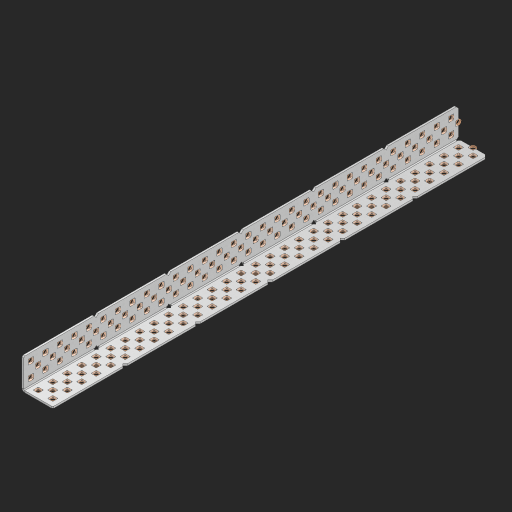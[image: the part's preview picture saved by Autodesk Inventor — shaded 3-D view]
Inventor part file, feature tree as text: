
AUTODESK INVENTOR PART (.ipt)
format: ipt  version: 2023 (Build 270158000, 158)  size: 1,938,432 bytes
history: native  units: in
note: dims shown in document units (in); Inventor stores cm internally (conversion verified against a paired STEP export)
features: other x186, extrude x178, sheet_metal_op x8, sketch x7, pattern_linear x2, mirror x1, chamfer x1
ambient origin geometry x8: Origin, YZ Plane, XZ Plane, XY Plane, X Axis, Y Axis, Z Axis, Center Point
bodies: Solid1 (feature_tree), Body (feature_tree)
feature tree (383):
  sheet_metal_op  "Flanges"
  sheet_metal_op  "Body Pattern"
  pattern_linear  "Center Pattern"  Spacing1=1.0in  [1 undecoded]
  other  "Arc Length"
  pattern_linear  "Notch Pattern"  Spacing1=0.25in  [1 undecoded]
  other  "Diagonal Plane"
  mirror  "Everything Mirrored"
  chamfer  "End Chamfer"
  sketch  "Sketch1"  dims[d0=1.0in]
  other  "Plate1"
  sketch  "Sketch2"  dims[d1=15.0in]
  other  "Plate2"
  sheet_metal_op  "Bend1"
  sheet_metal_op  "Corner1"
  sketch  "Sketch8"  dims[d2=0.0625in]
  sketch  "Sketch9"  dims[d3=0.0625in]
  other  "Srf91"
  sheet_metal_op  "Body Pattern Sketch"
  other  "Srf92"
  sketch  "Sketch13"  dims[d4=0.0312in]
  sketch  "Sketch15"  dims[d5=0.125in]
  sketch  "Sketch16"  dims[d6=0.0625in d7=1.0in d8=90.0deg d9=0.0312in d10=0.25in d11=0.0625in d12=0.0625in d49=0.182in d50=0.02in d52=0.25in d53=0.0625in d54=0.0in d55=0.172in d56=1.0in d57=0.0in d60=11.811in d62=0.5in d63=0.7874in d65=0.5in d85=0.1473in d86=0.1782in d89=0.0625in d90=0.0in d91=0.04in d92=0.0491in d95=2.5in d96=0.04in d97=0.25in d98=45.0deg d99=0.25in d106=0.182in d107=0.02in d108=0.5in d110=0.0625in d111=0.0in d112=0.172in d113=0.5in d114=0.0in d117=0.5in d123=0.25in d125=0.25in d126=0.0491in d127=0.1473in d128=0.08in d129=0.04in d130=2.5in]
  other  "Srf786"
  other  "Srf856"
  other  "Srf857"
  other  "Srf858"
  other  "Srf859"
  other  "Srf860"
  other  "Srf861"
  other  "Srf889"
  other  "Srf890"
  other  "Srf891"
  other  "Srf1275"
  other  "Srf1276"
  other  "Srf1278"
  other  "Srf1279"
  other  "Srf1280"
  other  "Srf1281"
  other  "Srf1282"
  other  "Srf1283"
  other  "Srf1277"
  other  "Srf1285"
  other  "Srf1286"
  other  "Srf1287"
  other  "Srf1383"
  other  "Srf1384"
  other  "Srf1385"
  other  "Srf1386"
  other  "Srf1387"
  other  "Srf1388"
  other  "Srf1389"
  other  "Srf1390"
  other  "Srf1391"
  other  "Srf1392"
  other  "Srf1393"
  other  "Srf1394"
  other  "Srf1395"
  other  "Srf1396"
  other  "Srf1397"
  other  "Srf1398"
  other  "Srf1399"
  other  "Srf1400"
  other  "Srf1401"
  other  "Srf1402"
  other  "Srf1403"
  other  "Srf1404"
  other  "Srf1405"
  other  "Srf1406"
  other  "Srf1407"
  other  "Srf1408"
  other  "Srf1409"
  other  "Srf1410"
  other  "Srf1411"
  other  "Srf1412"
  other  "Srf1413"
  other  "Srf1414"
  other  "Srf1415"
  other  "Srf1416"
  other  "Srf1417"
  other  "Srf1418"
  other  "Srf1419"
  other  "Srf1420"
  other  "Srf1421"
  other  "Srf1422"
  other  "Srf1423"
  other  "Srf1424"
  other  "Srf1425"
  other  "Srf1426"
  other  "Srf1427"
  other  "Srf1428"
  other  "Srf1429"
  other  "Srf1430"
  other  "Srf1431"
  other  "Srf1432"
  other  "Srf1433"
  other  "Srf1434"
  other  "Srf1445"
  other  "Srf1446"
  other  "Srf1447"
  other  "Srf1448"
  other  "Srf1449"
  other  "Srf1450"
  other  "Srf1451"
  other  "Srf1452"
  other  "Srf1453"
  other  "Srf1454"
  other  "Srf1455"
  other  "Srf1456"
  other  "Srf1457"
  other  "Srf1458"
  other  "Srf1459"
  other  "Srf1460"
  other  "Srf1461"
  other  "Srf1462"
  other  "Srf1463"
  other  "Srf1464"
  other  "Srf1465"
  other  "Srf1466"
  other  "Srf1467"
  other  "Srf1468"
  other  "Srf1469"
  other  "Srf1470"
  other  "Srf1475"
  other  "Srf1476"
  other  "Srf1477"
  other  "Srf1478"
  other  "Srf1479"
  other  "Srf1480"
  other  "Srf1481"
  other  "Srf1482"
  other  "Srf1483"
  other  "Srf1484"
  other  "Srf1485"
  other  "Srf1486"
  other  "Srf1487"
  other  "Srf1488"
  other  "Srf1489"
  other  "Srf1490"
  other  "Srf1491"
  other  "Srf1492"
  other  "Srf1493"
  other  "Srf1494"
  other  "Srf1495"
  other  "Srf1496"
  other  "Srf1497"
  other  "Srf1498"
  other  "Srf1499"
  other  "Srf1500"
  other  "Srf1501"
  other  "Srf1502"
  other  "Srf1503"
  other  "Srf1504"
  other  "Srf1505"
  other  "Srf1506"
  other  "Srf1507"
  other  "Srf1508"
  other  "Srf1509"
  other  "Srf1510"
  other  "Srf1511"
  other  "Srf1512"
  other  "Srf1513"
  other  "Srf1514"
  other  "Srf1515"
  other  "Srf1516"
  other  "Srf1517"
  other  "Srf1518"
  other  "Srf1519"
  other  "Srf1520"
  other  "Srf1521"
  other  "Srf1522"
  other  "Srf1523"
  other  "Srf1524"
  other  "Srf1525"
  other  "Srf1526"
  other  "Srf1537"
  other  "Srf1538"
  other  "Srf1539"
  other  "Srf1540"
  other  "Srf1541"
  other  "Srf1542"
  other  "Srf1543"
  other  "Srf1544"
  other  "Srf1545"
  other  "Srf1546"
  other  "Srf1547"
  other  "Srf1548"
  other  "Srf1549"
  other  "Srf1550"
  other  "Srf1551"
  other  "Srf1552"
  other  "Srf1553"
  other  "Srf1554"
  other  "Srf1555"
  other  "Srf1556"
  other  "Srf1557"
  other  "Srf1558"
  other  "Srf1559"
  other  "Srf1560"
  other  "Srf1561"
  other  "Srf1562"
  sheet_metal_op  "Body Stamp"
  sheet_metal_op  "Body Circle"
  other  "Center Stamp"
  other  "Center Circle"
  sheet_metal_op  "Notch"
  extrude  "ExtrusionSrf92"  Depth=0.0625in
  extrude  "ExtrusionSrf856"  Depth=0.0625in
  extrude  "ExtrusionSrf857"  Depth=2.5in
  extrude  "ExtrusionSrf858"  Depth=0.02in
  extrude  "ExtrusionSrf859"  Depth=2.5in
  extrude  "ExtrusionSrf860"  Depth=0.0625in
  extrude  "ExtrusionSrf861"  TaperAngle=0.0deg  [1 undecoded]
  extrude  "ExtrusionSrf889"  Depth=2.5in
  extrude  "ExtrusionSrf890"  Depth=1.0in TaperAngle=0.0deg
  extrude  "ExtrusionSrf891"  Depth=2.5in
  extrude  "ExtrusionSrf1275"  Depth=0.5in
  extrude  "ExtrusionSrf1276"  Depth=2.5in
  extrude  "ExtrusionSrf1277"  Depth=2.5in
  extrude  "ExtrusionSrf1278"  Depth=0.0625in
  extrude  "ExtrusionSrf1279"  Depth=2.5in TaperAngle=0.0deg
  extrude  "ExtrusionSrf1280"  Depth=2.5in
  extrude  "ExtrusionSrf1281"  Depth=2.5in TaperAngle=45.0deg
  extrude  "ExtrusionSrf1282"  Depth=2.5in
  extrude  "ExtrusionSrf1345"  Depth=2.5in
  extrude  "ExtrusionSrf1346"  Depth=0.02in
  extrude  "ExtrusionSrf1347"  Depth=0.5in
  extrude  "ExtrusionSrf1348"  Depth=0.0625in
  extrude  "ExtrusionSrf1383"  TaperAngle=0.0deg  [1 undecoded]
  extrude  "ExtrusionSrf1384"  Depth=2.5in
  extrude  "ExtrusionSrf1385"  Depth=0.5in TaperAngle=0.0deg
  extrude  "ExtrusionSrf1386"  Depth=0.5in
  extrude  "ExtrusionSrf1387"  Depth=2.5in
  extrude  "ExtrusionSrf1388"  Depth=2.5in
  extrude  "ExtrusionSrf1389"  Depth=2.5in
  extrude  "ExtrusionSrf1390"  Depth=2.5in
  extrude  "ExtrusionSrf1391"  Depth=2.5in
  extrude  "ExtrusionSrf1392"  Depth=2.5in
  extrude  "ExtrusionSrf1393"  Depth=2.5in
  extrude  "ExtrusionSrf1394"  [1 undecoded]
  extrude  "ExtrusionSrf1395"  [1 undecoded]
  extrude  "ExtrusionSrf1396"  [1 undecoded]
  extrude  "ExtrusionSrf1397"  [1 undecoded]
  extrude  "ExtrusionSrf1398"  [1 undecoded]
  extrude  "ExtrusionSrf1399"  [1 undecoded]
  extrude  "ExtrusionSrf1400"  [1 undecoded]
  extrude  "ExtrusionSrf1401"  [1 undecoded]
  extrude  "ExtrusionSrf1402"  [1 undecoded]
  extrude  "ExtrusionSrf1403"  [1 undecoded]
  extrude  "ExtrusionSrf1404"  [1 undecoded]
  extrude  "ExtrusionSrf1405"  [1 undecoded]
  extrude  "ExtrusionSrf1406"  [1 undecoded]
  extrude  "ExtrusionSrf1407"  [1 undecoded]
  extrude  "ExtrusionSrf1408"  [1 undecoded]
  extrude  "ExtrusionSrf1409"  [1 undecoded]
  extrude  "ExtrusionSrf1410"  [1 undecoded]
  extrude  "ExtrusionSrf1411"  [1 undecoded]
  extrude  "ExtrusionSrf1412"  [1 undecoded]
  extrude  "ExtrusionSrf1413"  [1 undecoded]
  extrude  "ExtrusionSrf1414"  [1 undecoded]
  extrude  "ExtrusionSrf1415"  [1 undecoded]
  extrude  "ExtrusionSrf1416"  [1 undecoded]
  extrude  "ExtrusionSrf1417"  [1 undecoded]
  extrude  "ExtrusionSrf1418"  [1 undecoded]
  extrude  "ExtrusionSrf1419"  [1 undecoded]
  extrude  "ExtrusionSrf1420"  [1 undecoded]
  extrude  "ExtrusionSrf1421"  [1 undecoded]
  extrude  "ExtrusionSrf1422"  [1 undecoded]
  extrude  "ExtrusionSrf1423"  [1 undecoded]
  extrude  "ExtrusionSrf1424"  [1 undecoded]
  extrude  "ExtrusionSrf1425"  [1 undecoded]
  extrude  "ExtrusionSrf1426"  [1 undecoded]
  extrude  "ExtrusionSrf1427"  [1 undecoded]
  extrude  "ExtrusionSrf1428"  [1 undecoded]
  extrude  "ExtrusionSrf1429"  [1 undecoded]
  extrude  "ExtrusionSrf1430"  [1 undecoded]
  extrude  "ExtrusionSrf1431"  [1 undecoded]
  extrude  "ExtrusionSrf1432"  [1 undecoded]
  extrude  "ExtrusionSrf1433"  [1 undecoded]
  extrude  "ExtrusionSrf1434"  [1 undecoded]
  extrude  "ExtrusionSrf1445"  [1 undecoded]
  extrude  "ExtrusionSrf1446"  [1 undecoded]
  extrude  "ExtrusionSrf1447"  [1 undecoded]
  extrude  "ExtrusionSrf1448"  [1 undecoded]
  extrude  "ExtrusionSrf1449"  [1 undecoded]
  extrude  "ExtrusionSrf1450"  [1 undecoded]
  extrude  "ExtrusionSrf1451"  [1 undecoded]
  extrude  "ExtrusionSrf1452"  [1 undecoded]
  extrude  "ExtrusionSrf1453"  [1 undecoded]
  extrude  "ExtrusionSrf1454"  [1 undecoded]
  extrude  "ExtrusionSrf1455"  [1 undecoded]
  extrude  "ExtrusionSrf1456"  [1 undecoded]
  extrude  "ExtrusionSrf1457"  [1 undecoded]
  extrude  "ExtrusionSrf1458"  [1 undecoded]
  extrude  "ExtrusionSrf1459"  [1 undecoded]
  extrude  "ExtrusionSrf1460"  [1 undecoded]
  extrude  "ExtrusionSrf1461"  [1 undecoded]
  extrude  "ExtrusionSrf1462"  [1 undecoded]
  extrude  "ExtrusionSrf1463"  [1 undecoded]
  extrude  "ExtrusionSrf1464"  [1 undecoded]
  extrude  "ExtrusionSrf1465"  [1 undecoded]
  extrude  "ExtrusionSrf1466"  [1 undecoded]
  extrude  "ExtrusionSrf1467"  [1 undecoded]
  extrude  "ExtrusionSrf1468"  [1 undecoded]
  extrude  "ExtrusionSrf1469"  [1 undecoded]
  extrude  "ExtrusionSrf1470"  [1 undecoded]
  extrude  "ExtrusionSrf1475"  [1 undecoded]
  extrude  "ExtrusionSrf1476"  [1 undecoded]
  extrude  "ExtrusionSrf1477"  [1 undecoded]
  extrude  "ExtrusionSrf1478"  [1 undecoded]
  extrude  "ExtrusionSrf1479"  [1 undecoded]
  extrude  "ExtrusionSrf1480"  [1 undecoded]
  extrude  "ExtrusionSrf1481"  [1 undecoded]
  extrude  "ExtrusionSrf1482"  [1 undecoded]
  extrude  "ExtrusionSrf1483"  [1 undecoded]
  extrude  "ExtrusionSrf1484"  [1 undecoded]
  extrude  "ExtrusionSrf1485"  [1 undecoded]
  extrude  "ExtrusionSrf1486"  [1 undecoded]
  extrude  "ExtrusionSrf1487"  [1 undecoded]
  extrude  "ExtrusionSrf1488"  [1 undecoded]
  extrude  "ExtrusionSrf1489"  [1 undecoded]
  extrude  "ExtrusionSrf1490"  [1 undecoded]
  extrude  "ExtrusionSrf1491"  [1 undecoded]
  extrude  "ExtrusionSrf1492"  [1 undecoded]
  extrude  "ExtrusionSrf1493"  [1 undecoded]
  extrude  "ExtrusionSrf1494"  [1 undecoded]
  extrude  "ExtrusionSrf1495"  [1 undecoded]
  extrude  "ExtrusionSrf1496"  [1 undecoded]
  extrude  "ExtrusionSrf1497"  [1 undecoded]
  extrude  "ExtrusionSrf1498"  [1 undecoded]
  extrude  "ExtrusionSrf1499"  [1 undecoded]
  extrude  "ExtrusionSrf1500"  [1 undecoded]
  extrude  "ExtrusionSrf1501"  [1 undecoded]
  extrude  "ExtrusionSrf1502"  [1 undecoded]
  extrude  "ExtrusionSrf1503"  [1 undecoded]
  extrude  "ExtrusionSrf1504"  [1 undecoded]
  extrude  "ExtrusionSrf1505"  [1 undecoded]
  extrude  "ExtrusionSrf1506"  [1 undecoded]
  extrude  "ExtrusionSrf1507"  [1 undecoded]
  extrude  "ExtrusionSrf1508"  [1 undecoded]
  extrude  "ExtrusionSrf1509"  [1 undecoded]
  extrude  "ExtrusionSrf1510"  [1 undecoded]
  extrude  "ExtrusionSrf1511"  [1 undecoded]
  extrude  "ExtrusionSrf1512"  [1 undecoded]
  extrude  "ExtrusionSrf1513"  [1 undecoded]
  extrude  "ExtrusionSrf1514"  [1 undecoded]
  extrude  "ExtrusionSrf1515"  [1 undecoded]
  extrude  "ExtrusionSrf1516"  [1 undecoded]
  extrude  "ExtrusionSrf1517"  [1 undecoded]
  extrude  "ExtrusionSrf1518"  [1 undecoded]
  extrude  "ExtrusionSrf1519"  [1 undecoded]
  extrude  "ExtrusionSrf1520"  [1 undecoded]
  extrude  "ExtrusionSrf1521"  [1 undecoded]
  extrude  "ExtrusionSrf1522"  [1 undecoded]
  extrude  "ExtrusionSrf1523"  [1 undecoded]
  extrude  "ExtrusionSrf1524"  [1 undecoded]
  extrude  "ExtrusionSrf1525"  [1 undecoded]
  extrude  "ExtrusionSrf1526"  [1 undecoded]
  extrude  "ExtrusionSrf1537"  [1 undecoded]
  extrude  "ExtrusionSrf1538"  [1 undecoded]
  extrude  "ExtrusionSrf1539"  [1 undecoded]
  extrude  "ExtrusionSrf1540"  [1 undecoded]
  extrude  "ExtrusionSrf1541"  [1 undecoded]
  extrude  "ExtrusionSrf1542"  [1 undecoded]
  extrude  "ExtrusionSrf1543"  [1 undecoded]
  extrude  "ExtrusionSrf1544"  [1 undecoded]
  extrude  "ExtrusionSrf1545"  [1 undecoded]
  extrude  "ExtrusionSrf1546"  [1 undecoded]
  extrude  "ExtrusionSrf1547"  [1 undecoded]
  extrude  "ExtrusionSrf1548"  [1 undecoded]
  extrude  "ExtrusionSrf1549"  [1 undecoded]
  extrude  "ExtrusionSrf1550"  [1 undecoded]
  extrude  "ExtrusionSrf1551"  [1 undecoded]
  extrude  "ExtrusionSrf1552"  [1 undecoded]
  extrude  "ExtrusionSrf1553"  [1 undecoded]
  extrude  "ExtrusionSrf1554"  [1 undecoded]
  extrude  "ExtrusionSrf1555"  [1 undecoded]
  extrude  "ExtrusionSrf1556"  [1 undecoded]
  extrude  "ExtrusionSrf1557"  [1 undecoded]
  extrude  "ExtrusionSrf1558"  [1 undecoded]
  extrude  "ExtrusionSrf1559"  [1 undecoded]
  extrude  "ExtrusionSrf1560"  [1 undecoded]
  extrude  "ExtrusionSrf1561"  [1 undecoded]
  extrude  "ExtrusionSrf1562"  [1 undecoded]
note: 149 required parameter values undecoded (feature->parameter linkage not recoverable at this tier; creation-order binding heuristic only, values carry confidence <= 0.55)
